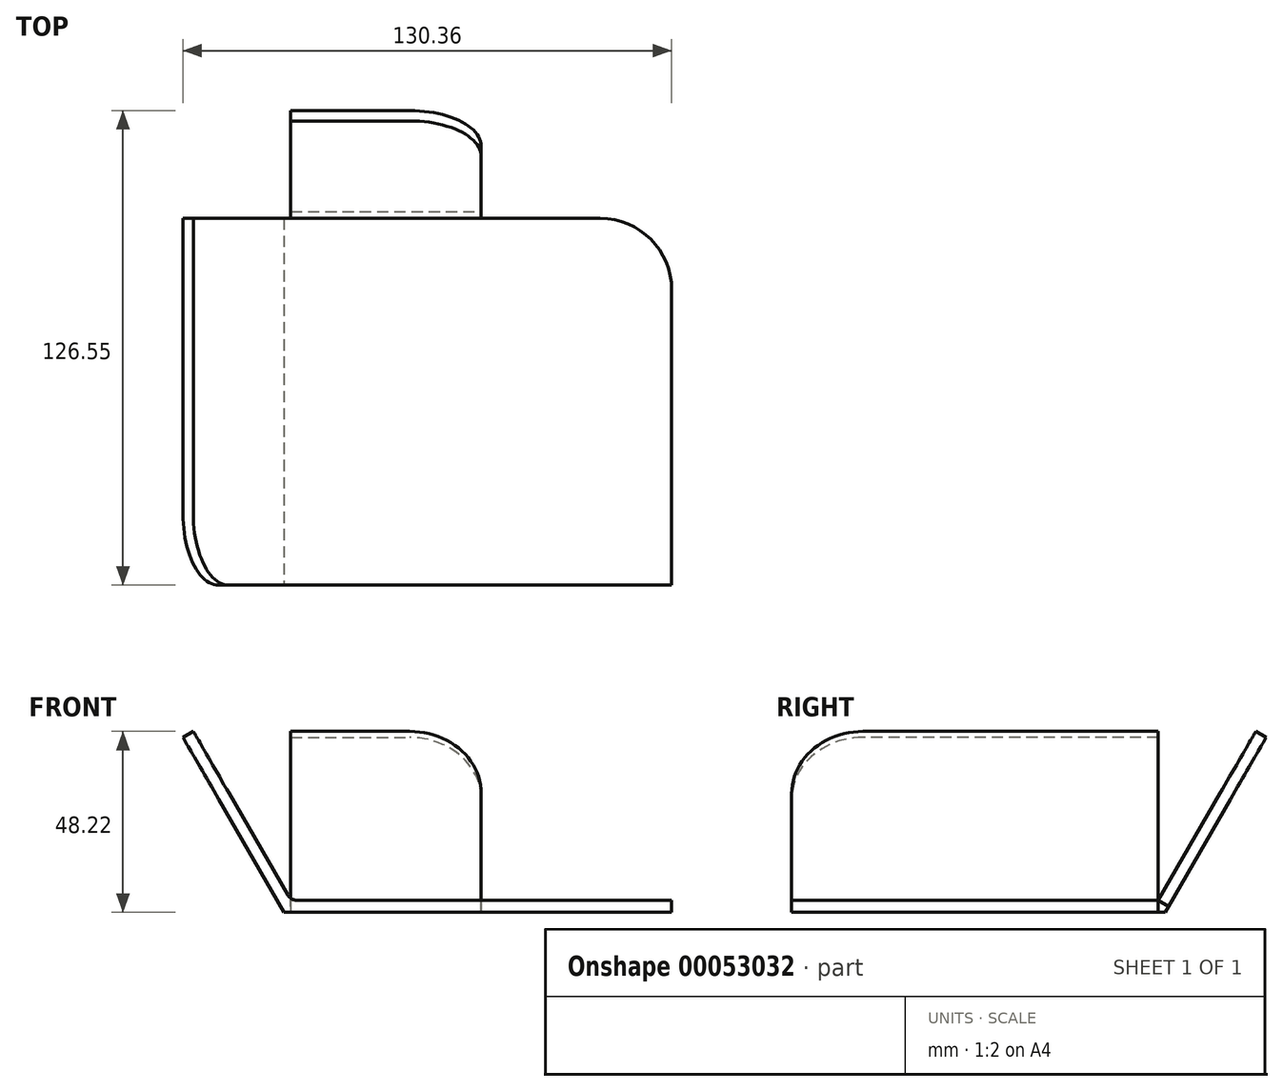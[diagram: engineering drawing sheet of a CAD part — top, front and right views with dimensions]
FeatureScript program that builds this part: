
annotation { "Feature Type Name" : "Feature", "Feature Type Description" : "" }
export const myFeature = defineFeature(function(context is Context, id is Id, definition is map)
    precondition{}
    {
        {
            var Q0;
            Q0=qCreatedBy(makeId("Top.planeOp"),FACE);
            var sketch = newSketch(context, id + "F0", { "sketchPlane" : qUnion([Q0])});
            skLineSegment(sketch, "E0.bottom", {"start": v(0, 0) * mm, "end": v(-155.45, 0) * mm});
            skLineSegment(sketch, "E0.top", {"start": v(0, 151.64) * mm, "end": v(-155.45, 151.64) * mm});
            skLineSegment(sketch, "E0.left", {"start": v(0, 0) * mm, "end": v(0, 151.64) * mm});
            skLineSegment(sketch, "E0.right", {"start": v(-155.45, 0) * mm, "end": v(-155.45, 151.64) * mm});
            skSolve(sketch);
        }
        {
            var Q0;
            Q0 = qSketchRegion(id + "F0", true);
            extrude(context, id + "F1", {"entities" : qUnion([Q0]), "depth" : 50.8 * mm});
        }
        {
            var Q0;
            Q0=makeQuery(id+"F1.opExtrude","SWEPT_FACE",FACE,{"disambiguationData":[OSD([sQuery(id+"F0.wireOp",EDGE,"E0.bottom")])]});
            var sketch = newSketch(context, id + "F2", { "sketchPlane" : qUnion([Q0])});
            skLineSegment(sketch, "E1", {"start": v(0, 0) * mm, "end": v(-103.43, 0) * mm});
            skLineSegment(sketch, "E2", {"start": v(-103.43, 0) * mm, "end": v(-130.36, 46.63) * mm});
            skLineSegment(sketch, "E3", {"start": v(-130.36, 46.63) * mm, "end": v(-127.6, 48.22) * mm});
            skLineSegment(sketch, "E4", {"start": v(-127.6, 48.22) * mm, "end": v(-101.6, 3.17) * mm});
            skLineSegment(sketch, "E5", {"start": v(-101.6, 3.17) * mm, "end": v(0, 3.18) * mm});
            skLineSegment(sketch, "E6", {"start": v(0, 3.18) * mm, "end": v(0, 0) * mm});
            skSolve(sketch);
        }
        {
            var Q0;
            {var subQ3=sQuery(id+"F2.wireOp",EDGE,"E2");Q0=makeQuery(id+"F2.imprint","IMPRINT",FACE,{"disambiguationData":[TD([[makeQuery(id+"F2.imprint","IMPRINT",EDGE,{"derivedFrom":subQ3}),1.0]])]});}
            extrude(context, id + "F3", {"entities" : qUnion([Q0]), "operationType" : NewBodyOperationType.REMOVE, "oppositeDirection" : true, "depth" : 97.8 * mm});
        }
        {
            var Q0;
            Q0=makeQuery(id+"F1.opExtrude","SWEPT_FACE",FACE,{"disambiguationData":[OSD([sQuery(id+"F0.wireOp",EDGE,"E0.left")])]});
            var sketch = newSketch(context, id + "F4", { "sketchPlane" : qUnion([Q0])});
            skLineSegment(sketch, "E7", {"start": v(98.67, 4.7) * mm, "end": v(123.8, 48.22) * mm});
            skLineSegment(sketch, "E8", {"start": v(123.8, 48.22) * mm, "end": v(126.55, 46.63) * mm});
            skLineSegment(sketch, "E9", {"start": v(126.55, 46.63) * mm, "end": v(99.62, 0) * mm});
            skLineSegment(sketch, "E10", {"start": v(99.62, 0) * mm, "end": v(0, 0) * mm});
            skLineSegment(sketch, "E11", {"start": v(0, 0) * mm, "end": v(0, 3.18) * mm});
            skLineSegment(sketch, "E12", {"start": v(0, 3.18) * mm, "end": v(96.03, 3.18) * mm});
            skPoint(sketch, "E13.visualSharp", {"position": v(97.8, 3.18) * mm});
            skLineSegment(sketch, "E14", {"start": v(98.67, 4.7) * mm, "end": v(97.8, 3.18) * mm});
            skSolve(sketch);
        }
        {
            var Q0;
            Q0=makeQuery(id+"F4.imprint","IMPRINT",FACE,{"disambiguationData":[TD([[makeQuery(id+"F4.imprint","IMPRINT",EDGE,{"derivedFrom":sQuery(id+"F4.wireOp",EDGE,"E7")}),1.0]])]});
            extrude(context, id + "F5", {"entities" : qUnion([Q0]), "operationType" : NewBodyOperationType.REMOVE, "endBound" : BoundingType.THROUGH_ALL, "oppositeDirection" : true, "depth" : 103.38 * mm});
        }
        {
            var Q0;
            Q0=makeQuery(id+"F5.boolean.opBoolean","COPY",FACE,{"derivedFrom":makeQuery(id+"F5.opExtrude","SWEPT_FACE",FACE,{"disambiguationData":[OSD([sQuery(id+"F4.wireOp",EDGE,"E7")])]})});
            var sketch = newSketch(context, id + "F6", { "sketchPlane" : qUnion([Q0])});
            skLineSegment(sketch, "E15", {"start": v(-101.62, 103.66) * mm, "end": v(-69.87, 103.66) * mm});
            skLineSegment(sketch, "E16", {"start": v(-50.82, 84.6) * mm, "end": v(-50.82, 51.64) * mm});
            skPoint(sketch, "E17.visualSharp", {"position": v(-50.82, 103.66) * mm});
            skArc(sketch, "E17.filletArc", {"start": v(-50.82, 84.6) * mm, "mid": v(-56.4, 98.08) * mm, "end": v(-69.87, 103.66) * mm});
            skLineSegment(sketch, "E18", {"start": v(-101.6, 51.64) * mm, "end": v(-101.62, 103.66) * mm});
            skLineSegment(sketch, "E19", {"start": v(-101.6, 51.64) * mm, "end": v(-50.82, 51.64) * mm});
            skSolve(sketch);
        }
        {
            var Q0;
            {var subQ3=sQuery(id+"F6.wireOp",EDGE,"E18");Q0=makeQuery(id+"F6.imprint","IMPRINT",FACE,{"disambiguationData":[TD([[makeQuery(id+"F6.imprint","IMPRINT",EDGE,{"derivedFrom":subQ3}),1.0]])]});}
            var Q1;
            {var subQ4=sQuery(id+"F6.wireOp",EDGE,"E16");Q1=makeQuery(id+"F6.imprint","IMPRINT",FACE,{"disambiguationData":[TD([[makeQuery(id+"F6.imprint","IMPRINT",EDGE,{"derivedFrom":subQ4}),1.0]])]});}
            extrude(context, id + "F7", {"entities" : qUnion([Q0, Q1]), "operationType" : NewBodyOperationType.REMOVE, "oppositeDirection" : true, "depth" : 25.4 * mm});
        }
        {
            var Q0;
            Q0=makeQuery(id+"F3.boolean.opBoolean","COPY",FACE,{"derivedFrom":makeQuery(id+"F3.opExtrude","SWEPT_FACE",FACE,{"disambiguationData":[OSD([sQuery(id+"F2.wireOp",EDGE,"E4")])]})});
            var sketch = newSketch(context, id + "F8", { "sketchPlane" : qUnion([Q0])});
            skLineSegment(sketch, "E20", {"start": v(97.8, 53.55) * mm, "end": v(97.8, 105.56) * mm});
            skLineSegment(sketch, "E21", {"start": v(97.8, 105.56) * mm, "end": v(19.05, 105.56) * mm});
            skLineSegment(sketch, "E22", {"start": v(0, 86.51) * mm, "end": v(0, 53.55) * mm});
            skLineSegment(sketch, "E23", {"start": v(0, 53.55) * mm, "end": v(97.8, 53.55) * mm});
            skPoint(sketch, "E24.visualSharp", {"position": v(0, 105.56) * mm});
            skArc(sketch, "E24.filletArc", {"start": v(19.05, 105.56) * mm, "mid": v(5.58, 99.98) * mm, "end": v(0, 86.51) * mm});
            skSolve(sketch);
        }
        {
            var Q0;
            {var subQ0=sQuery(id+"F8.wireOp",EDGE,"E24.filletArc");Q0=makeQuery(id+"F8.imprint","IMPRINT",FACE,{"disambiguationData":[TD([[makeQuery(id+"F8.imprint","IMPRINT",EDGE,{"derivedFrom":subQ0}),-1.0]])]});}
            extrude(context, id + "F9", {"entities" : qUnion([Q0]), "operationType" : NewBodyOperationType.REMOVE, "oppositeDirection" : true, "depth" : 25.4 * mm});
        }
        {
            var Q0;
            Q0=makeQuery(id+"F1.opExtrude","CAP_FACE",FACE,{"disambiguationData":[OSD([sQuery(id+"F0.wireOp",EDGE,"E0.bottom"),sQuery(id+"F0.wireOp",EDGE,"E0.top"),sQuery(id+"F0.wireOp",EDGE,"E0.left"),sQuery(id+"F0.wireOp",EDGE,"E0.right")])],"isStart":true});
            var sketch = newSketch(context, id + "F10", { "sketchPlane" : qUnion([Q0])});
            skLineSegment(sketch, "E25.top", {"start": v(0, -97.8) * mm, "end": v(-50.8, -97.8) * mm});
            skLineSegment(sketch, "E26.bottom", {"start": v(-155.45, -97.8) * mm, "end": v(-101.6, -97.8) * mm});
            skLineSegment(sketch, "E26.top", {"start": v(-155.45, -102.19) * mm, "end": v(-101.6, -102.19) * mm});
            skLineSegment(sketch, "E26.left", {"start": v(-155.45, -97.8) * mm, "end": v(-155.45, -102.19) * mm});
            skLineSegment(sketch, "E26.right", {"start": v(-101.6, -97.8) * mm, "end": v(-101.6, -102.19) * mm});
            skLineSegment(sketch, "E27", {"start": v(0, -97.8) * mm, "end": v(0, -103.35) * mm});
            skLineSegment(sketch, "E28", {"start": v(0, -103.35) * mm, "end": v(-50.8, -103.35) * mm});
            skLineSegment(sketch, "E29", {"start": v(-50.8, -103.35) * mm, "end": v(-50.8, -97.8) * mm});
            skSolve(sketch);
        }
        {
            var Q0;
            {var subQ0=sQuery(id+"F10.wireOp",EDGE,"E26.right");var subQ1=sQuery(id+"F10.wireOp",EDGE,"E26.bottom");var subQ2=makeQuery(id+"F10.imprint","INTERSECT",VERTEX,{"derivedFrom":[subQ1,subQ0]});Q0=makeQuery(id+"F10.imprint","IMPRINT",FACE,{"disambiguationData":[TD([[makeQuery(id+"F10.imprint","IMPRINT",EDGE,{"disambiguationData":[TD([[subQ2,1.0]])],"derivedFrom":subQ1}),-1.0]])]});}
            var Q1;
            {var subQ0=sQuery(id+"F10.wireOp",EDGE,"E26.top");Q1=makeQuery(id+"F10.imprint","IMPRINT",FACE,{"disambiguationData":[TD([[makeQuery(id+"F10.imprint","IMPRINT",EDGE,{"derivedFrom":subQ0}),1.0]])]});}
            var Q2;
            {var subQ3=sQuery(id+"F10.wireOp",EDGE,"E28");Q2=makeQuery(id+"F10.imprint","IMPRINT",FACE,{"disambiguationData":[TD([[makeQuery(id+"F10.imprint","IMPRINT",EDGE,{"derivedFrom":subQ3}),-1.0]])]});}
            var Q3;
            {var subQ0=sQuery(id+"F10.wireOp",EDGE,"E25.top");Q3=makeQuery(id+"F10.imprint","IMPRINT",FACE,{"disambiguationData":[TD([[makeQuery(id+"F10.imprint","IMPRINT",EDGE,{"derivedFrom":subQ0}),1.0]])]});}
            extrude(context, id + "F11", {"entities" : qUnion([Q0, Q1, Q2, Q3]), "operationType" : NewBodyOperationType.REMOVE, "oppositeDirection" : true, "depth" : 76.2 * mm});
        }
        {
            var Q0;
            Q0=makeQuery(id+"F3.boolean.opBoolean","COPY",EDGE,{"derivedFrom":makeQuery(id+"F3.opExtrude","SWEPT_EDGE",EDGE,{"disambiguationData":[OSD([sQuery(id+"F2.wireOp",EDGE,"E4"),sQuery(id+"F2.wireOp",EDGE,"E5")])]})});
            var Q1;
            Q1=makeQuery(id+"F3.boolean.opBoolean","COPY",EDGE,{"derivedFrom":makeQuery(id+"F3.opExtrude","SWEPT_EDGE",EDGE,{"disambiguationData":[OSD([sQuery(id+"F0.wireOp",EDGE,"E0.bottom"),sQuery(id+"F2.wireOp",EDGE,"E1"),sQuery(id+"F2.wireOp",EDGE,"E2")])]})});
            var Q2;
            Q2=makeQuery(id+"F5.boolean.opBoolean","COPY",EDGE,{"derivedFrom":makeQuery(id+"F5.opExtrude","SWEPT_EDGE",EDGE,{"disambiguationData":[OSD([sQuery(id+"F0.wireOp",EDGE,"E0.left"),sQuery(id+"F4.wireOp",EDGE,"E9"),sQuery(id+"F4.wireOp",EDGE,"E10")])]})});
            fillet(context, id + "F12", {"entities" : qUnion([Q0, Q1, Q2]), "radius" : 3.05 * mm, "tangentPropagation" : true, "allowEdgeOverflow" : false});
        }
        {
            var Q0;
            Q0=makeQuery(id+"F3.boolean.opBoolean","COPY",FACE,{"derivedFrom":makeQuery(id+"F3.opExtrude","SWEPT_FACE",FACE,{"disambiguationData":[OSD([sQuery(id+"F2.wireOp",EDGE,"E5")])]})});
            var sketch = newSketch(context, id + "F13", { "sketchPlane" : qUnion([Q0])});
            skLineSegment(sketch, "E30.bottom", {"start": v(-99.84, 97.8) * mm, "end": v(-19.05, 97.8) * mm});
            skLineSegment(sketch, "E30.top", {"start": v(-99.84, 0) * mm, "end": v(0, 0) * mm});
            skLineSegment(sketch, "E30.left", {"start": v(-99.84, 97.8) * mm, "end": v(-99.84, 0) * mm});
            skLineSegment(sketch, "E30.right", {"start": v(0, 78.74) * mm, "end": v(0, 0) * mm});
            skPoint(sketch, "E31.visualSharp", {"position": v(0, 97.8) * mm});
            skArc(sketch, "E31.filletArc", {"start": v(0, 78.74) * mm, "mid": v(-5.58, 92.21) * mm, "end": v(-19.05, 97.8) * mm});
            skSolve(sketch);
        }
        {
            var Q0;
            {var subQ0=sQuery(id+"F13.wireOp",EDGE,"E31.filletArc");Q0=makeQuery(id+"F13.imprint","IMPRINT",FACE,{"disambiguationData":[TD([[makeQuery(id+"F13.imprint","IMPRINT",EDGE,{"derivedFrom":subQ0}),-1.0]])]});}
            extrude(context, id + "F14", {"entities" : qUnion([Q0]), "operationType" : NewBodyOperationType.REMOVE, "oppositeDirection" : true, "depth" : 25.4 * mm});
        }
    });
